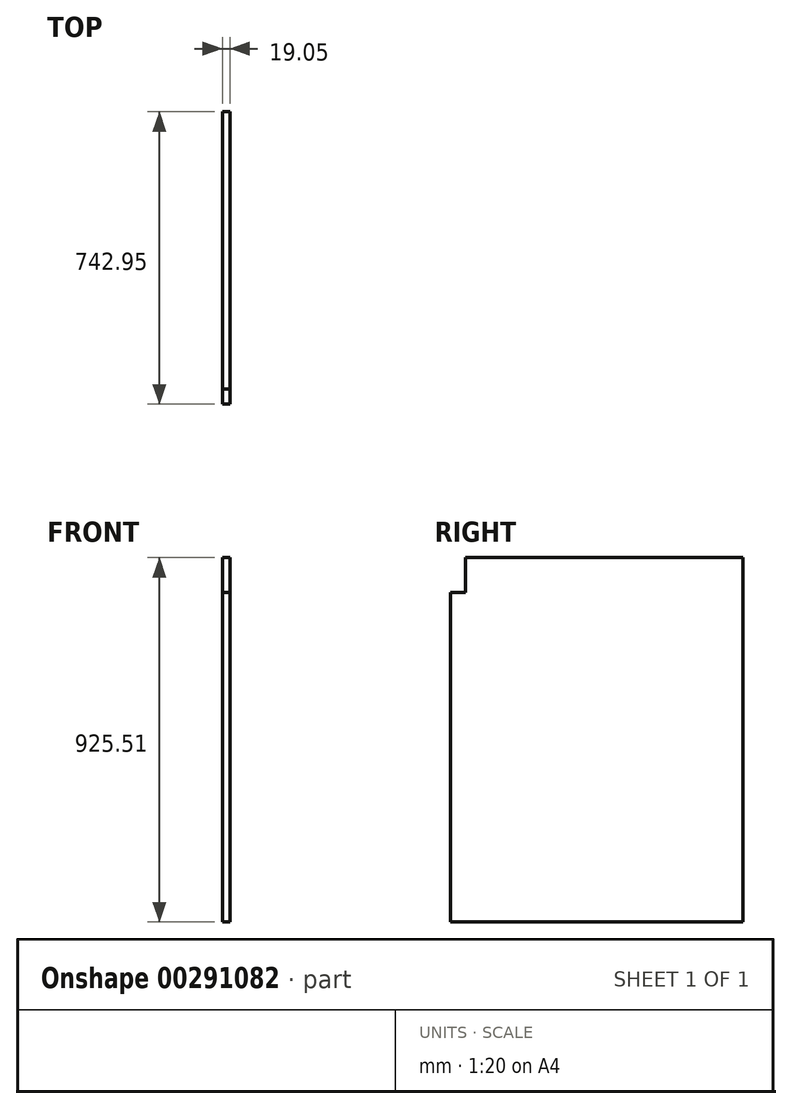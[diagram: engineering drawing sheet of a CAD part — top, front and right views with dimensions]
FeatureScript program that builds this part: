
annotation { "Feature Type Name" : "Feature", "Feature Type Description" : "" }
export const myFeature = defineFeature(function(context is Context, id is Id, definition is map)
    precondition{}
    {
        {
            var Q0;
            Q0=qCreatedBy(makeId("Right.planeOp"),FACE);
            var sketch = newSketch(context, id + "F0", { "sketchPlane" : qUnion([Q0])});
            skLineSegment(sketch, "E0.bottom", {"start": v(0, 0) * mm, "end": v(742.95, 0) * mm});
            skLineSegment(sketch, "E0.top", {"start": v(0, -925.51) * mm, "end": v(742.95, -925.51) * mm});
            skLineSegment(sketch, "E0.left", {"start": v(0, 0) * mm, "end": v(0, -925.51) * mm});
            skLineSegment(sketch, "E0.right", {"start": v(742.95, 0) * mm, "end": v(742.95, -925.51) * mm});
            skPoint(sketch, "E1.firstSnap0", {"position": v(0, -462.76) * mm});
            skPoint(sketch, "E1.oppositeSnap0", {"position": v(0, -462.76) * mm});
            skSolve(sketch);
        }
        {
            var Q0;
            Q0 = qSketchRegion(id + "F0", true);
            extrude(context, id + "F1", {"entities" : qUnion([Q0]), "depth" : 19.05 * mm});
        }
        {
            var Q0;
            Q0=qCreatedBy(makeId("Right.planeOp"),FACE);
            var sketch = newSketch(context, id + "F2", { "sketchPlane" : qUnion([Q0])});
            skLineSegment(sketch, "E2.bottom", {"start": v(0, 0) * mm, "end": v(38.1, 0) * mm});
            skLineSegment(sketch, "E2.top", {"start": v(0, -88.9) * mm, "end": v(38.1, -88.9) * mm});
            skLineSegment(sketch, "E2.left", {"start": v(0, 0) * mm, "end": v(0, -88.9) * mm});
            skLineSegment(sketch, "E2.right", {"start": v(38.1, 0) * mm, "end": v(38.1, -88.9) * mm});
            skSolve(sketch);
        }
        {
            var Q0;
            Q0 = qSketchRegion(id + "F2", true);
            extrude(context, id + "F3", {"entities" : qUnion([Q0]), "operationType" : NewBodyOperationType.REMOVE, "endBound" : BoundingType.THROUGH_ALL, "depth" : 25.4 * mm});
        }
    });
